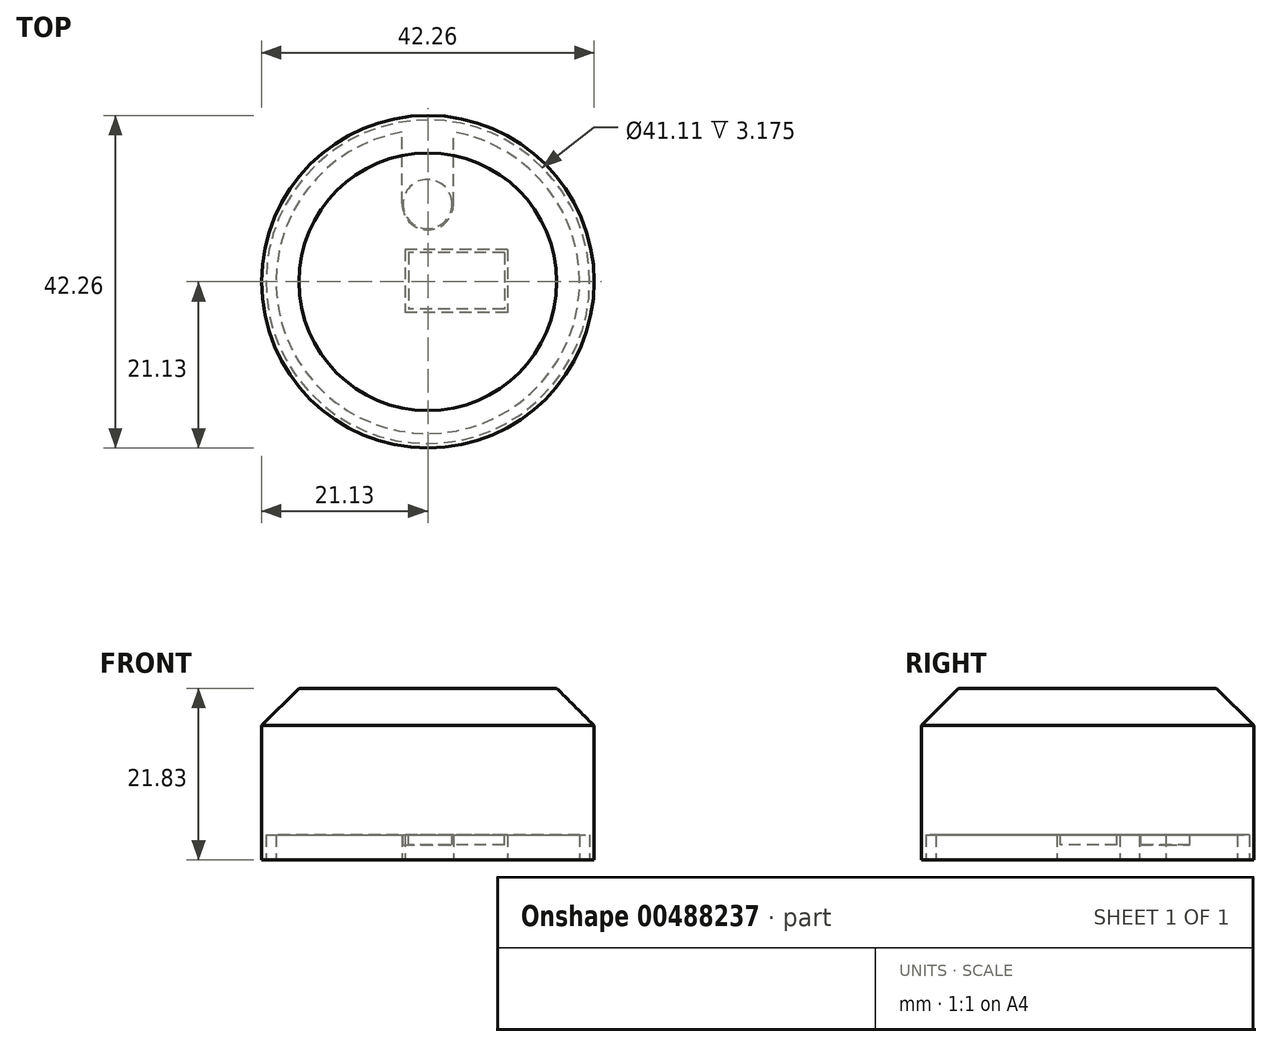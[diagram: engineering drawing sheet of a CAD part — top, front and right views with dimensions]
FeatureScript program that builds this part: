
annotation { "Feature Type Name" : "Feature", "Feature Type Description" : "" }
export const myFeature = defineFeature(function(context is Context, id is Id, definition is map)
    precondition{}
    {
        {
            var Q0;
            Q0=qCreatedBy(makeId("Top.planeOp"),FACE);
            var sketch = newSketch(context, id + "F0", { "sketchPlane" : qUnion([Q0])});
            skCircle(sketch, "E0", {"center": v(0, 0) * mm, "radius": 21.12 * mm});
            skSolve(sketch);
        }
        {
            var Q0;
            Q0 = qSketchRegion(id + "F0", true);
            extrude(context, id + "F1", {"entities" : qUnion([Q0]), "depth" : 21.83 * mm});
        }
        {
            var Q0;
            Q0=makeQuery(id+"F1.opExtrude","CAP_EDGE",EDGE,{"disambiguationData":[OSD([sQuery(id+"F0.wireOp",EDGE,"E0")])],"isStart":false});
            chamfer(context, id + "F2", {"entities" : qUnion([Q0]), "width" : 4.75 * mm, "tangentPropagation" : true});
        }
        {
            var Q0;
            Q0=makeQuery(id+"F1.opExtrude","CAP_FACE",FACE,{"disambiguationData":[OSD([sQuery(id+"F0.wireOp",EDGE,"E0")])],"isStart":true});
            var sketch = newSketch(context, id + "F3", { "sketchPlane" : qUnion([Q0])});
            skCircle(sketch, "E1", {"center": v(0, -9.88) * mm, "radius": 3.26 * mm});
            skLineSegment(sketch, "E2.bottom", {"start": v(10.13, -4.12) * mm, "end": v(-2.87, -4.13) * mm});
            skLineSegment(sketch, "E2.top", {"start": v(10.12, 3.88) * mm, "end": v(-2.87, 3.87) * mm});
            skLineSegment(sketch, "E2.left", {"start": v(10.13, -4.12) * mm, "end": v(10.12, 3.88) * mm});
            skLineSegment(sketch, "E2.right", {"start": v(-2.87, -4.13) * mm, "end": v(-2.87, 3.87) * mm});
            skCircle(sketch, "E3", {"center": v(0, 0) * mm, "radius": 20.56 * mm});
            skArc(sketch, "E4", {"start": v(3.26, -19) * mm, "mid": v(0, 19.28) * mm, "end": v(-3.26, -19) * mm});
            skLineSegment(sketch, "E5", {"start": v(-3.26, -9.96) * mm, "end": v(-3.26, -19) * mm});
            skLineSegment(sketch, "E6", {"start": v(3.26, -9.88) * mm, "end": v(3.26, -19) * mm});
            skSolve(sketch);
        }
        {
            var Q0;
            {var subQ0=sQuery(id+"F3.wireOp",EDGE,"E1");var subQ1=makeQuery(id+"F3.imprint","INTERSECT",VERTEX,{"derivedFrom":[subQ0,sQuery(id+"F3.wireOp",EDGE,"E5")]});Q0=makeQuery(id+"F3.imprint","IMPRINT",FACE,{"disambiguationData":[TD([[makeQuery(id+"F3.imprint","IMPRINT",EDGE,{"disambiguationData":[TD([[subQ1,-1.0]])],"derivedFrom":subQ0}),1.0]])]});}
            var Q1;
            Q1=makeQuery(id+"F3.imprint","IMPRINT",FACE,{"disambiguationData":[TD([[makeQuery(id+"F3.imprint","IMPRINT",EDGE,{"derivedFrom":sQuery(id+"F3.wireOp",EDGE,"E3")}),1.0]])]});
            var Q2;
            Q2=makeQuery(id+"F3.imprint","IMPRINT",FACE,{"disambiguationData":[TD([[makeQuery(id+"F3.imprint","IMPRINT",EDGE,{"derivedFrom":sQuery(id+"F3.wireOp",EDGE,"E2.bottom")}),-1.0]])]});
            extrude(context, id + "F4", {"entities" : qUnion([Q0, Q1, Q2]), "operationType" : NewBodyOperationType.REMOVE, "oppositeDirection" : true, "depth" : 3.17 * mm});
        }
        {
            var Q0;
            Q0=makeQuery(id+"F4.boolean.opBoolean","COPY",FACE,{"derivedFrom":makeQuery(id+"F4.opExtrude","CAP_FACE",FACE,{"disambiguationData":[OSD([sQuery(id+"F3.wireOp",EDGE,"E1"),sQuery(id+"F3.wireOp",EDGE,"E3"),sQuery(id+"F3.wireOp",EDGE,"E4"),sQuery(id+"F3.wireOp",EDGE,"E5"),sQuery(id+"F3.wireOp",EDGE,"E6")])],"isStart":false})});
            var sketch = newSketch(context, id + "F5", { "sketchPlane" : qUnion([Q0])});
            skCircle(sketch, "E7", {"center": v(-0.04, -9.88) * mm, "radius": 3.12 * mm});
            skPoint(sketch, "E7.centerSnap0", {"position": v(-0.04, -6.61) * mm});
            skLineSegment(sketch, "E8.0", {"start": v(9.72, 3.47) * mm, "end": v(-2.47, 3.47) * mm});
            skLineSegment(sketch, "E8.1", {"start": v(9.72, -3.72) * mm, "end": v(9.72, 3.47) * mm});
            skLineSegment(sketch, "E8.2", {"start": v(9.72, -3.72) * mm, "end": v(-2.47, -3.72) * mm});
            skLineSegment(sketch, "E8.3", {"start": v(-2.47, -3.72) * mm, "end": v(-2.47, 3.47) * mm});
            skSolve(sketch);
        }
        {
            var Q0;
            Q0=makeQuery(id+"F5.imprint","IMPRINT",FACE,{"disambiguationData":[TD([[makeQuery(id+"F5.imprint","IMPRINT",EDGE,{"derivedFrom":sQuery(id+"F5.wireOp",EDGE,"E8.0")}),1.0]])]});
            var Q1;
            Q1=makeQuery(id+"F5.imprint","IMPRINT",FACE,{"disambiguationData":[TD([[makeQuery(id+"F5.imprint","IMPRINT",EDGE,{"derivedFrom":sQuery(id+"F5.wireOp",EDGE,"E7")}),1.0]])]});
            var Q2;
            Q2=sQuery(id+"F5.wireOp",EDGE,"E7");
            var Q3;
            Q3=sQuery(id+"F5.wireOp",EDGE,"E8.2");
            extrude(context, id + "F6", {"entities" : qUnion([Q0, Q1]), "operationType" : NewBodyOperationType.ADD, "surfaceEntities" : qUnion([Q2, Q3]), "depth" : 1.27 * mm});
        }
    });
